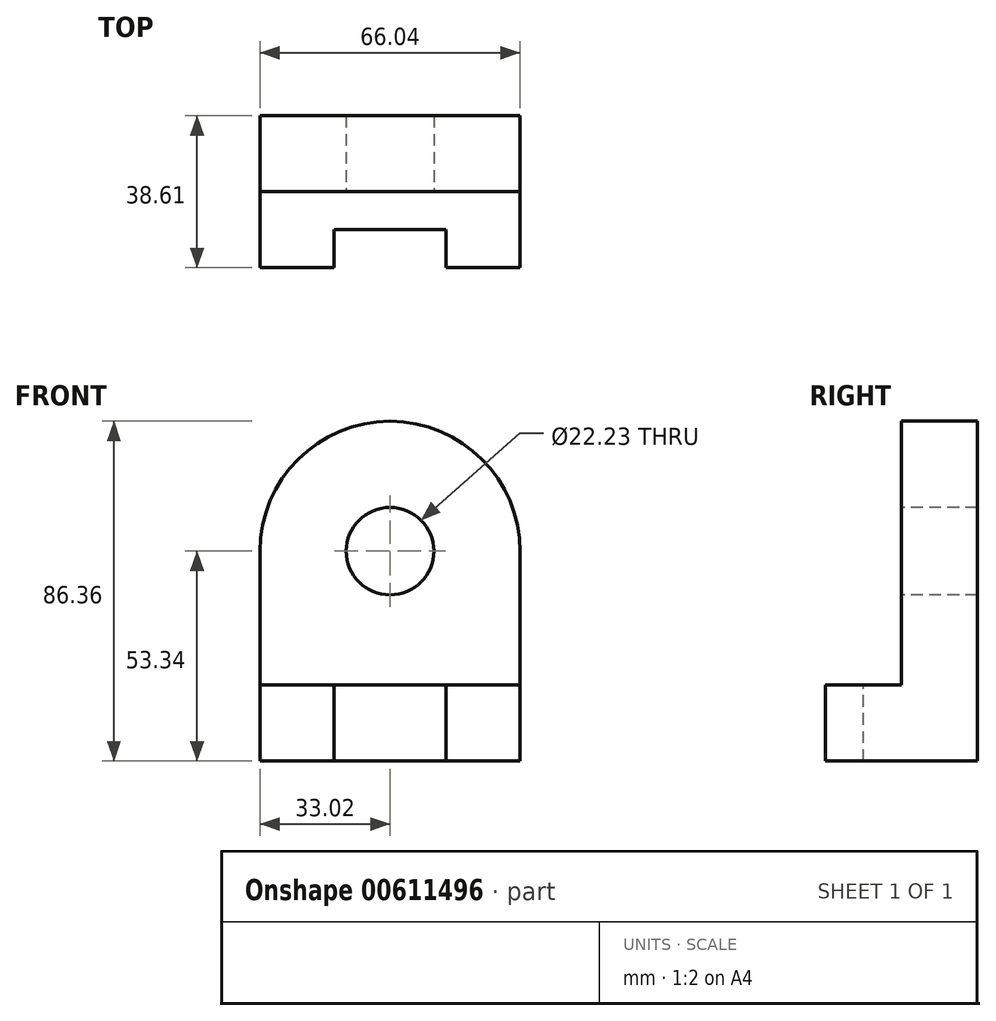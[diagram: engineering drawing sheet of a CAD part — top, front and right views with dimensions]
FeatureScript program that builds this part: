
annotation { "Feature Type Name" : "Feature", "Feature Type Description" : "" }
export const myFeature = defineFeature(function(context is Context, id is Id, definition is map)
    precondition{}
    {
        {
            var Q0;
            Q0=qCreatedBy(makeId("Front.planeOp"),FACE);
            var sketch = newSketch(context, id + "F0", { "sketchPlane" : qUnion([Q0])});
            skLineSegment(sketch, "E0", {"start": v(0, 0) * mm, "end": v(66.04, 0) * mm});
            skLineSegment(sketch, "E1", {"start": v(66.04, 0) * mm, "end": v(66.04, 86.36) * mm});
            skLineSegment(sketch, "E2", {"start": v(0, 0) * mm, "end": v(0, 86.36) * mm});
            skLineSegment(sketch, "E3", {"start": v(0, 86.36) * mm, "end": v(66.04, 86.36) * mm});
            skSolve(sketch);
        }
        {
            var Q0;
            Q0=makeQuery(id+"F0.imprint","IMPRINT",FACE,{"disambiguationData":[TD([[makeQuery(id+"F0.imprint","IMPRINT",EDGE,{"derivedFrom":sQuery(id+"F0.wireOp",EDGE,"E0")}),1.0]])]});
            extrude(context, id + "F1", {"entities" : qUnion([Q0]), "depth" : 19.3 * mm, "offsetDistance" : 25.4 * mm});
        }
        {
            var Q0;
            Q0=makeQuery(id+"F1.opExtrude","SWEPT_EDGE",EDGE,{"disambiguationData":[OSD([sQuery(id+"F0.wireOp",EDGE,"E1"),sQuery(id+"F0.wireOp",EDGE,"E3")])]});
            var Q1;
            Q1=makeQuery(id+"F1.opExtrude","SWEPT_EDGE",EDGE,{"disambiguationData":[OSD([sQuery(id+"F0.wireOp",EDGE,"E2"),sQuery(id+"F0.wireOp",EDGE,"E3")])]});
            fillet(context, id + "F2", {"entities" : qUnion([Q0, Q1]), "radius" : 33.02 * mm, "tangentPropagation" : true, "allowEdgeOverflow" : false});
        }
        {
            var Q0;
            Q0=qCreatedBy(makeId("Front.planeOp"),FACE);
            var sketch = newSketch(context, id + "F3", { "sketchPlane" : qUnion([Q0])});
            skLineSegment(sketch, "E4", {"start": v(0, 0) * mm, "end": v(0, 19.3) * mm});
            skLineSegment(sketch, "E5", {"start": v(0, 19.3) * mm, "end": v(66.04, 19.3) * mm});
            skLineSegment(sketch, "E6", {"start": v(66.04, 19.3) * mm, "end": v(66.04, 0) * mm});
            skLineSegment(sketch, "E7", {"start": v(66.04, 0) * mm, "end": v(0, 0) * mm});
            skSolve(sketch);
        }
        {
            var Q0;
            Q0=makeQuery(id+"F3.imprint","IMPRINT",FACE,{"disambiguationData":[TD([[makeQuery(id+"F3.imprint","IMPRINT",EDGE,{"derivedFrom":sQuery(id+"F3.wireOp",EDGE,"E4")}),-1.0]])]});
            extrude(context, id + "F4", {"entities" : qUnion([Q0]), "operationType" : NewBodyOperationType.ADD, "depth" : 19.3 * mm, "offsetDistance" : 25.4 * mm});
        }
        {
            var Q0;
            Q0=makeQuery(id+"F1.opExtrude","CAP_FACE",FACE,{"disambiguationData":[OSD([sQuery(id+"F0.wireOp",EDGE,"E0"),sQuery(id+"F0.wireOp",EDGE,"E1"),sQuery(id+"F0.wireOp",EDGE,"E2"),sQuery(id+"F0.wireOp",EDGE,"E3")])],"isStart":false});
            var sketch = newSketch(context, id + "F5", { "sketchPlane" : qUnion([Q0])});
            skLineSegment(sketch, "E8.bottom", {"start": v(0, 0) * mm, "end": v(66.04, 0) * mm});
            skLineSegment(sketch, "E8.top", {"start": v(0, 19.3) * mm, "end": v(66.04, 19.3) * mm});
            skLineSegment(sketch, "E8.left", {"start": v(0, 0) * mm, "end": v(0, 19.3) * mm});
            skLineSegment(sketch, "E8.right", {"start": v(66.04, 0) * mm, "end": v(66.04, 19.3) * mm});
            skSolve(sketch);
        }
        {
            var Q0;
            Q0=makeQuery(id+"F5.imprint","IMPRINT",FACE,{"disambiguationData":[TD([[makeQuery(id+"F5.imprint","IMPRINT",EDGE,{"derivedFrom":sQuery(id+"F5.wireOp",EDGE,"E8.bottom")}),1.0]])]});
            extrude(context, id + "F6", {"entities" : qUnion([Q0]), "operationType" : NewBodyOperationType.ADD, "depth" : 9.65 * mm, "offsetDistance" : 25.4 * mm});
        }
        {
            var Q0;
            Q0=makeQuery(id+"F6.opExtrude","CAP_FACE",FACE,{"disambiguationData":[OSD([sQuery(id+"F5.wireOp",EDGE,"E8.bottom"),sQuery(id+"F5.wireOp",EDGE,"E8.top"),sQuery(id+"F5.wireOp",EDGE,"E8.left"),sQuery(id+"F5.wireOp",EDGE,"E8.right")])],"isStart":false});
            var sketch = newSketch(context, id + "F7", { "sketchPlane" : qUnion([Q0])});
            skLineSegment(sketch, "E9.bottom", {"start": v(0, 0) * mm, "end": v(18.8, 0) * mm});
            skLineSegment(sketch, "E9.top", {"start": v(0, 19.3) * mm, "end": v(18.8, 19.3) * mm});
            skLineSegment(sketch, "E9.left", {"start": v(0, 0) * mm, "end": v(0, 19.3) * mm});
            skLineSegment(sketch, "E9.right", {"start": v(18.8, 0) * mm, "end": v(18.8, 19.3) * mm});
            skLineSegment(sketch, "E10.bottom", {"start": v(66.04, 0) * mm, "end": v(47.24, 0) * mm});
            skLineSegment(sketch, "E10.top", {"start": v(66.04, 19.3) * mm, "end": v(47.24, 19.3) * mm});
            skLineSegment(sketch, "E10.left", {"start": v(66.04, 0) * mm, "end": v(66.04, 19.3) * mm});
            skLineSegment(sketch, "E10.right", {"start": v(47.24, 0) * mm, "end": v(47.24, 19.3) * mm});
            skSolve(sketch);
        }
        {
            var Q0;
            Q0=makeQuery(id+"F7.imprint","IMPRINT",FACE,{"disambiguationData":[TD([[makeQuery(id+"F7.imprint","IMPRINT",EDGE,{"derivedFrom":sQuery(id+"F7.wireOp",EDGE,"E9.bottom")}),1.0]])]});
            var Q1;
            Q1=makeQuery(id+"F7.imprint","IMPRINT",FACE,{"disambiguationData":[TD([[makeQuery(id+"F7.imprint","IMPRINT",EDGE,{"derivedFrom":sQuery(id+"F7.wireOp",EDGE,"E10.bottom")}),1.0]])]});
            extrude(context, id + "F8", {"entities" : qUnion([Q0, Q1]), "operationType" : NewBodyOperationType.ADD, "depth" : 9.65 * mm, "offsetDistance" : 25.4 * mm});
        }
        {
            var Q0;
            Q0=makeQuery(id+"F1.opExtrude","CAP_FACE",FACE,{"disambiguationData":[OSD([sQuery(id+"F0.wireOp",EDGE,"E0"),sQuery(id+"F0.wireOp",EDGE,"E1"),sQuery(id+"F0.wireOp",EDGE,"E2"),sQuery(id+"F0.wireOp",EDGE,"E3")])],"isStart":false});
            var sketch = newSketch(context, id + "F9", { "sketchPlane" : qUnion([Q0])});
            skCircle(sketch, "E11", {"center": v(33.02, 53.34) * mm, "radius": 11.11 * mm});
            skSolve(sketch);
        }
        {
            var Q0;
            Q0=sQuery(id+"F9.wireOp",VERTEX,"E11.center");
            var Q1;
            Q1=makeQuery(id+"F1.opExtrude","SWEPT_BODY",BODY,{"disambiguationData":[OSD([sQuery(id+"F0.wireOp",EDGE,"E0"),sQuery(id+"F0.wireOp",EDGE,"E1"),sQuery(id+"F0.wireOp",EDGE,"E2"),sQuery(id+"F0.wireOp",EDGE,"E3")])]});
            hole(context, id + "F10", {"style" : HoleStyle.SIMPLE, "endStyle" : HoleEndStyle.THROUGH, "holeDiameter" : 22.22 * mm, "majorDiameter" : 6.35 * mm, "isTappedThrough" : true, "tappedDepth" : 12.7 * mm, "tapClearance" : 3, "locations" : qUnion([Q0]), "scope" : qUnion([Q1])});
        }
    });
